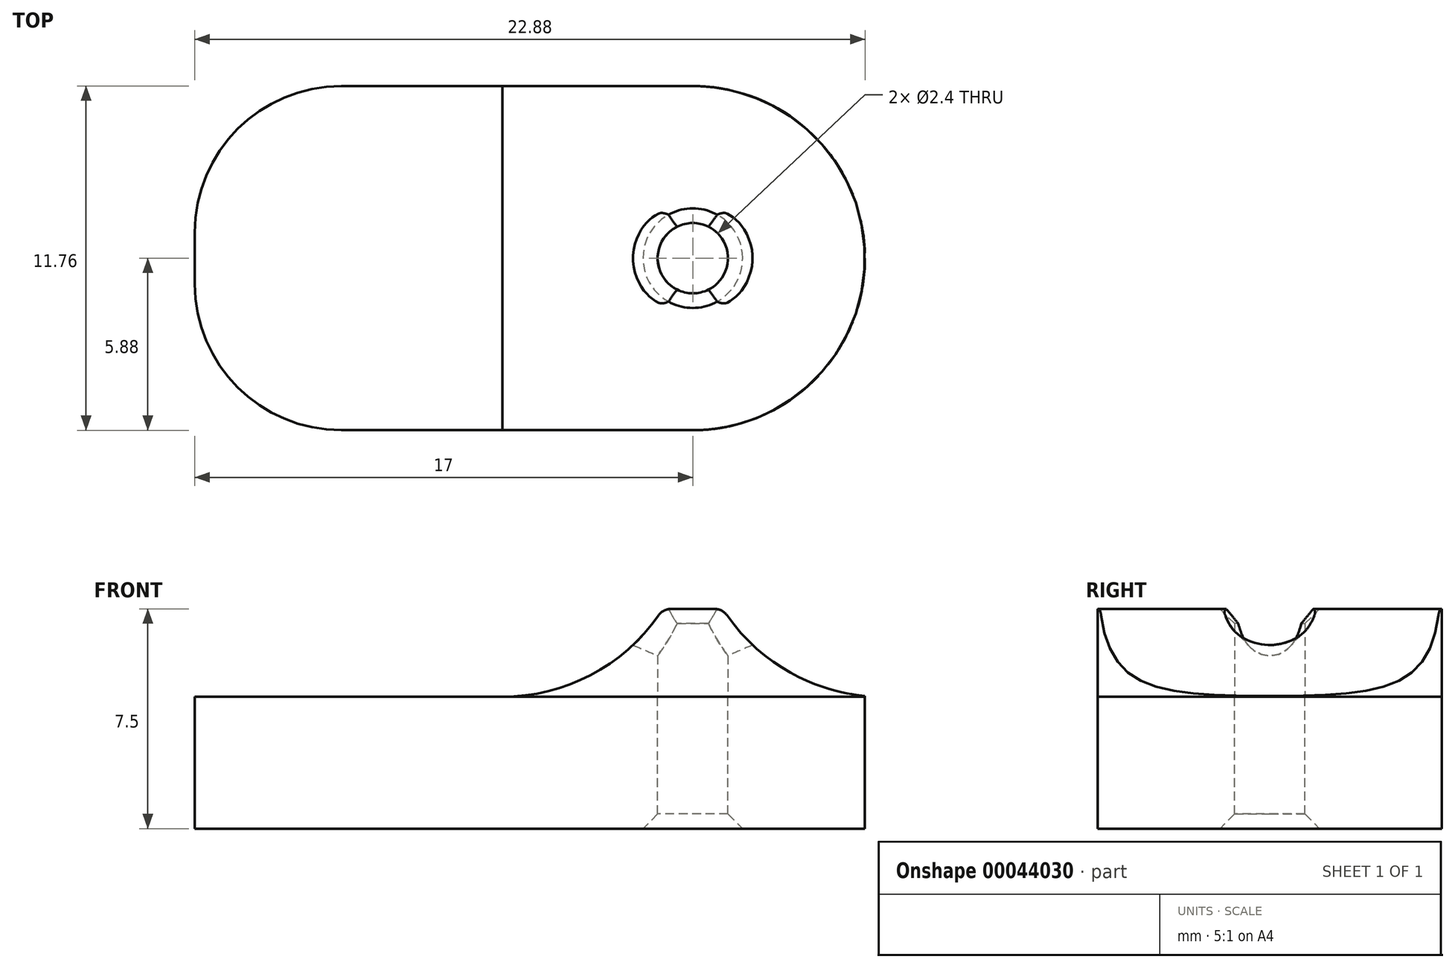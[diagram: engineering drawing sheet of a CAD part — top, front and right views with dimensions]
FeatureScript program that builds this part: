
annotation { "Feature Type Name" : "Feature", "Feature Type Description" : "" }
export const myFeature = defineFeature(function(context is Context, id is Id, definition is map)
    precondition{}
    {
        {
            var Q0;
            Q0=qCreatedBy(makeId("Top.planeOp"),FACE);
            var sketch = newSketch(context, id + "F0", { "sketchPlane" : qUnion([Q0])});
            skCircle(sketch, "E0", {"center": v(0, 0) * mm, "radius": 1.2 * mm});
            skCircle(sketch, "E1", {"center": v(0, 0) * mm, "radius": 2 * mm});
            skLineSegment(sketch, "E2.bottom", {"start": v(-12, 5.88) * mm, "end": v(0, 5.88) * mm});
            skLineSegment(sketch, "E2.top", {"start": v(-12, -5.88) * mm, "end": v(0, -5.88) * mm});
            skLineSegment(sketch, "E2.left", {"start": v(-17, 0.87) * mm, "end": v(-17, -0.87) * mm});
            skPoint(sketch, "E3.visualSharp", {"position": v(-17, 5.88) * mm});
            skArc(sketch, "E3.filletArc", {"start": v(-12, 5.88) * mm, "mid": v(-15.54, 4.41) * mm, "end": v(-17, 0.87) * mm});
            skPoint(sketch, "E4.visualSharp", {"position": v(-17, -5.88) * mm});
            skArc(sketch, "E4.filletArc", {"start": v(-17, -0.88) * mm, "mid": v(-15.54, -4.41) * mm, "end": v(-12, -5.88) * mm});
            skArc(sketch, "E5", {"start": v(0, -5.88) * mm, "mid": v(5.88, 0) * mm, "end": v(0, 5.88) * mm});
            skLineSegment(sketch, "E6.bottom", {"start": v(0, -5.88) * mm, "end": v(5.9, -5.88) * mm});
            skLineSegment(sketch, "E6.top", {"start": v(0, 5.88) * mm, "end": v(5.9, 5.88) * mm});
            skLineSegment(sketch, "E6.right", {"start": v(5.9, -5.88) * mm, "end": v(5.9, 5.88) * mm});
            skSolve(sketch);
        }
        {
            var Q0;
            Q0=makeQuery(id+"F0.imprint","IMPRINT",FACE,{"disambiguationData":[TD([[makeQuery(id+"F0.imprint","IMPRINT",EDGE,{"derivedFrom":sQuery(id+"F0.wireOp",EDGE,"E1")}),-1.0]])]});
            var Q1;
            Q1=makeQuery(id+"F0.imprint","IMPRINT",FACE,{"disambiguationData":[TD([[makeQuery(id+"F0.imprint","IMPRINT",EDGE,{"derivedFrom":sQuery(id+"F0.wireOp",EDGE,"E0")}),-1.0]])]});
            extrude(context, id + "F1", {"entities" : qUnion([Q0, Q1]), "oppositeDirection" : true, "depth" : 4.5 * mm});
        }
        {
            var Q0;
            Q0=qCreatedBy(makeId("Front.planeOp"),FACE);
            var sketch = newSketch(context, id + "F2", { "sketchPlane" : qUnion([Q0])});
            skLineSegment(sketch, "E7", {"start": v(0, 0) * mm, "end": v(6.5, 0) * mm, "construction": true});
            skArc(sketch, "E8", {"start": v(1.02, 3) * mm, "mid": v(3.11, 0.95) * mm, "end": v(5.89, 0.03) * mm});
            skArc(sketch, "E9.1.0.0", {"start": v(-6.5, 0) * mm, "mid": v(-3.38, 0.8) * mm, "end": v(-1.02, 3) * mm});
            skLineSegment(sketch, "E10.top", {"start": v(5.89, 0) * mm, "end": v(-6.5, 0) * mm});
            skLineSegment(sketch, "E11", {"start": v(5.89, 0) * mm, "end": v(5.89, 0.03) * mm});
            skLineSegment(sketch, "E12", {"start": v(1.02, 3) * mm, "end": v(-1.02, 3) * mm});
            skSolve(sketch);
        }
        {
            var Q0;
            Q0=makeQuery(id+"F2.imprint","IMPRINT",FACE,{"disambiguationData":[TD([[makeQuery(id+"F2.imprint","IMPRINT",EDGE,{"derivedFrom":sQuery(id+"F2.wireOp",EDGE,"E8")}),-1.0]])]});
            extrude(context, id + "F3", {"entities" : qUnion([Q0]), "endBound" : BoundingType.SYMMETRIC, "depth" : 11.75 * mm});
        }
        {
            var Q0;
            Q0=makeQuery(id+"F0.imprint","IMPRINT",FACE,{"disambiguationData":[TD([[makeQuery(id+"F0.imprint","IMPRINT",EDGE,{"derivedFrom":sQuery(id+"F0.wireOp",EDGE,"E0")}),1.0]])]});
            extrude(context, id + "F4", {"entities" : qUnion([Q0]), "operationType" : NewBodyOperationType.REMOVE, "depth" : 6.5 * mm});
        }
        {
            var Q0;
            Q0=makeQuery(id+"F4.boolean.opBoolean","INTERSECT",EDGE,{"disambiguationData":[OD(0.0)],"derivedFrom":[makeQuery(id+"F3.opExtrude","SWEPT_FACE",FACE,{"disambiguationData":[OSD([sQuery(id+"F2.wireOp",EDGE,"E12")])]}),makeQuery(id+"F4.opExtrude","SWEPT_FACE",FACE,{"disambiguationData":[OSD([sQuery(id+"F0.wireOp",EDGE,"E0")])]})]});
            var Q1;
            Q1=makeQuery(id+"F4.boolean.opBoolean","INTERSECT",EDGE,{"disambiguationData":[OD(1.0)],"derivedFrom":[makeQuery(id+"F3.opExtrude","SWEPT_FACE",FACE,{"disambiguationData":[OSD([sQuery(id+"F2.wireOp",EDGE,"E12")])]}),makeQuery(id+"F4.opExtrude","SWEPT_FACE",FACE,{"disambiguationData":[OSD([sQuery(id+"F0.wireOp",EDGE,"E0")])]})]});
            var Q2;
            Q2=makeQuery(id+"F4.boolean.opBoolean","INTERSECT",EDGE,{"derivedFrom":[makeQuery(id+"F3.opExtrude","SWEPT_FACE",FACE,{"disambiguationData":[OSD([sQuery(id+"F2.wireOp",EDGE,"E9.1.0.0")])]}),makeQuery(id+"F4.opExtrude","SWEPT_FACE",FACE,{"disambiguationData":[OSD([sQuery(id+"F0.wireOp",EDGE,"E0")])]})]});
            var Q3;
            Q3=makeQuery(id+"F4.boolean.opBoolean","INTERSECT",EDGE,{"derivedFrom":[makeQuery(id+"F3.opExtrude","SWEPT_FACE",FACE,{"disambiguationData":[OSD([sQuery(id+"F2.wireOp",EDGE,"E8")])]}),makeQuery(id+"F4.opExtrude","SWEPT_FACE",FACE,{"disambiguationData":[OSD([sQuery(id+"F0.wireOp",EDGE,"E0")])]})]});
            chamfer(context, id + "F5", {"entities" : qUnion([Q0, Q1, Q2, Q3]), "width" : 0.5 * mm, "tangentPropagation" : true});
        }
        {
            var Q0;
            Q0=makeQuery(id+"F1.opExtrude","CAP_EDGE",EDGE,{"disambiguationData":[OSD([sQuery(id+"F0.wireOp",EDGE,"E0")])],"isStart":false});
            chamfer(context, id + "F6", {"entities" : qUnion([Q0]), "width" : 0.5 * mm, "tangentPropagation" : true});
        }
        {
            var Q0;
            {var subQ4=sQuery(id+"F0.wireOp",EDGE,"E6.bottom");Q0=makeQuery(id+"F0.imprint","IMPRINT",FACE,{"disambiguationData":[TD([[makeQuery(id+"F0.imprint","IMPRINT",EDGE,{"derivedFrom":subQ4}),1.0]])]});}
            extrude(context, id + "F7", {"entities" : qUnion([Q0]), "operationType" : NewBodyOperationType.REMOVE, "depth" : 3 * mm});
        }
        {
            var Q0;
            {var subQ0=sQuery(id+"F2.wireOp",EDGE,"E8");var subQ1=sQuery(id+"F2.wireOp",EDGE,"E12");Q0=makeQuery(id+"F4.boolean.opBoolean","SPLIT",EDGE,{"disambiguationData":[TD([makeQuery(id+"F3.opExtrude","CAP_FACE",FACE,{"disambiguationData":[OSD([subQ0,sQuery(id+"F2.wireOp",EDGE,"E9.1.0.0"),sQuery(id+"F2.wireOp",EDGE,"E10.top"),sQuery(id+"F2.wireOp",EDGE,"E11"),subQ1])],"isStart":false})])],"derivedFrom":makeQuery(id+"F3.opExtrude","SWEPT_EDGE",EDGE,{"disambiguationData":[OSD([subQ0,subQ1])]})});}
            var Q1;
            {var subQ0=sQuery(id+"F2.wireOp",EDGE,"E9.1.0.0");var subQ1=sQuery(id+"F2.wireOp",EDGE,"E12");Q1=makeQuery(id+"F4.boolean.opBoolean","SPLIT",EDGE,{"disambiguationData":[TD([makeQuery(id+"F3.opExtrude","CAP_FACE",FACE,{"disambiguationData":[OSD([sQuery(id+"F2.wireOp",EDGE,"E8"),subQ0,sQuery(id+"F2.wireOp",EDGE,"E10.top"),sQuery(id+"F2.wireOp",EDGE,"E11"),subQ1])],"isStart":false})])],"derivedFrom":makeQuery(id+"F3.opExtrude","SWEPT_EDGE",EDGE,{"disambiguationData":[OSD([subQ0,subQ1])]})});}
            var Q2;
            {var subQ0=sQuery(id+"F2.wireOp",EDGE,"E8");var subQ1=sQuery(id+"F2.wireOp",EDGE,"E12");Q2=makeQuery(id+"F4.boolean.opBoolean","SPLIT",EDGE,{"disambiguationData":[TD([makeQuery(id+"F3.opExtrude","CAP_FACE",FACE,{"disambiguationData":[OSD([subQ0,sQuery(id+"F2.wireOp",EDGE,"E9.1.0.0"),sQuery(id+"F2.wireOp",EDGE,"E10.top"),sQuery(id+"F2.wireOp",EDGE,"E11"),subQ1])],"isStart":true})])],"derivedFrom":makeQuery(id+"F3.opExtrude","SWEPT_EDGE",EDGE,{"disambiguationData":[OSD([subQ0,subQ1])]})});}
            var Q3;
            {var subQ0=sQuery(id+"F2.wireOp",EDGE,"E9.1.0.0");var subQ1=sQuery(id+"F2.wireOp",EDGE,"E12");Q3=makeQuery(id+"F4.boolean.opBoolean","SPLIT",EDGE,{"disambiguationData":[TD([makeQuery(id+"F3.opExtrude","CAP_FACE",FACE,{"disambiguationData":[OSD([sQuery(id+"F2.wireOp",EDGE,"E8"),subQ0,sQuery(id+"F2.wireOp",EDGE,"E10.top"),sQuery(id+"F2.wireOp",EDGE,"E11"),subQ1])],"isStart":true})])],"derivedFrom":makeQuery(id+"F3.opExtrude","SWEPT_EDGE",EDGE,{"disambiguationData":[OSD([subQ0,subQ1])]})});}
            fillet(context, id + "F8", {"entities" : qUnion([Q0, Q1, Q2, Q3]), "radius" : 0.5 * mm, "tangentPropagation" : true, "allowEdgeOverflow" : false});
        }
    });
